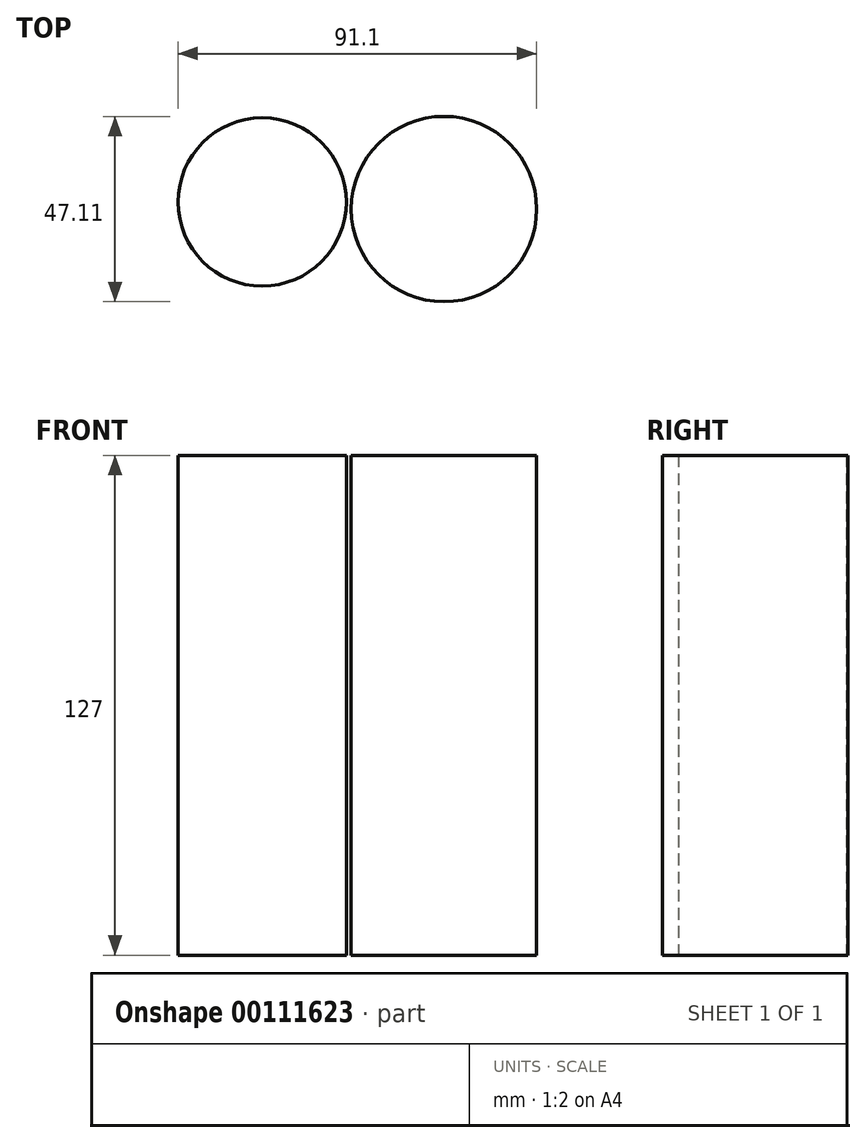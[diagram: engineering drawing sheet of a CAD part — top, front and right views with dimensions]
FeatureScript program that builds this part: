
annotation { "Feature Type Name" : "Feature", "Feature Type Description" : "" }
export const myFeature = defineFeature(function(context is Context, id is Id, definition is map)
    precondition{}
    {
        {
            var Q0;
            Q0=qCreatedBy(makeId("Top.planeOp"),FACE);
            var sketch = newSketch(context, id + "F0", { "sketchPlane" : qUnion([Q0])});
            skCircle(sketch, "E0", {"center": v(-36.14, 27.27) * mm, "radius": 21.37 * mm});
            skCircle(sketch, "E1", {"center": v(10.02, 25.47) * mm, "radius": 23.56 * mm});
            skSolve(sketch);
        }
        {
            var Q0;
            Q0=makeQuery(id+"F0.imprint","IMPRINT",FACE,{"disambiguationData":[TD([[makeQuery(id+"F0.imprint","IMPRINT",EDGE,{"derivedFrom":sQuery(id+"F0.wireOp",EDGE,"E0")}),1.0]])]});
            var Q1;
            Q1=makeQuery(id+"F0.imprint","IMPRINT",FACE,{"disambiguationData":[TD([[makeQuery(id+"F0.imprint","IMPRINT",EDGE,{"derivedFrom":sQuery(id+"F0.wireOp",EDGE,"E1")}),1.0]])]});
            extrude(context, id + "F1", {"entities" : qUnion([Q0, Q1]), "depth" : 127 * mm});
        }
        {
            var Q0;
            Q0=qCreatedBy(makeId("Top.planeOp"),FACE);
            var sketch = newSketch(context, id + "F2", { "sketchPlane" : qUnion([Q0])});
            skCircle(sketch, "E2", {"center": v(3.45, 31.05) * mm, "radius": 19.8 * mm});
            skSolve(sketch);
        }
        {
            var Q0;
            Q0=sQuery(id+"F2.wireOp",EDGE,"E2");
            extrude(context, id + "F3", {"bodyType" : ToolBodyType.SURFACE, "surfaceEntities" : qUnion([Q0]), "depth" : 304.8 * mm});
        }
    });
